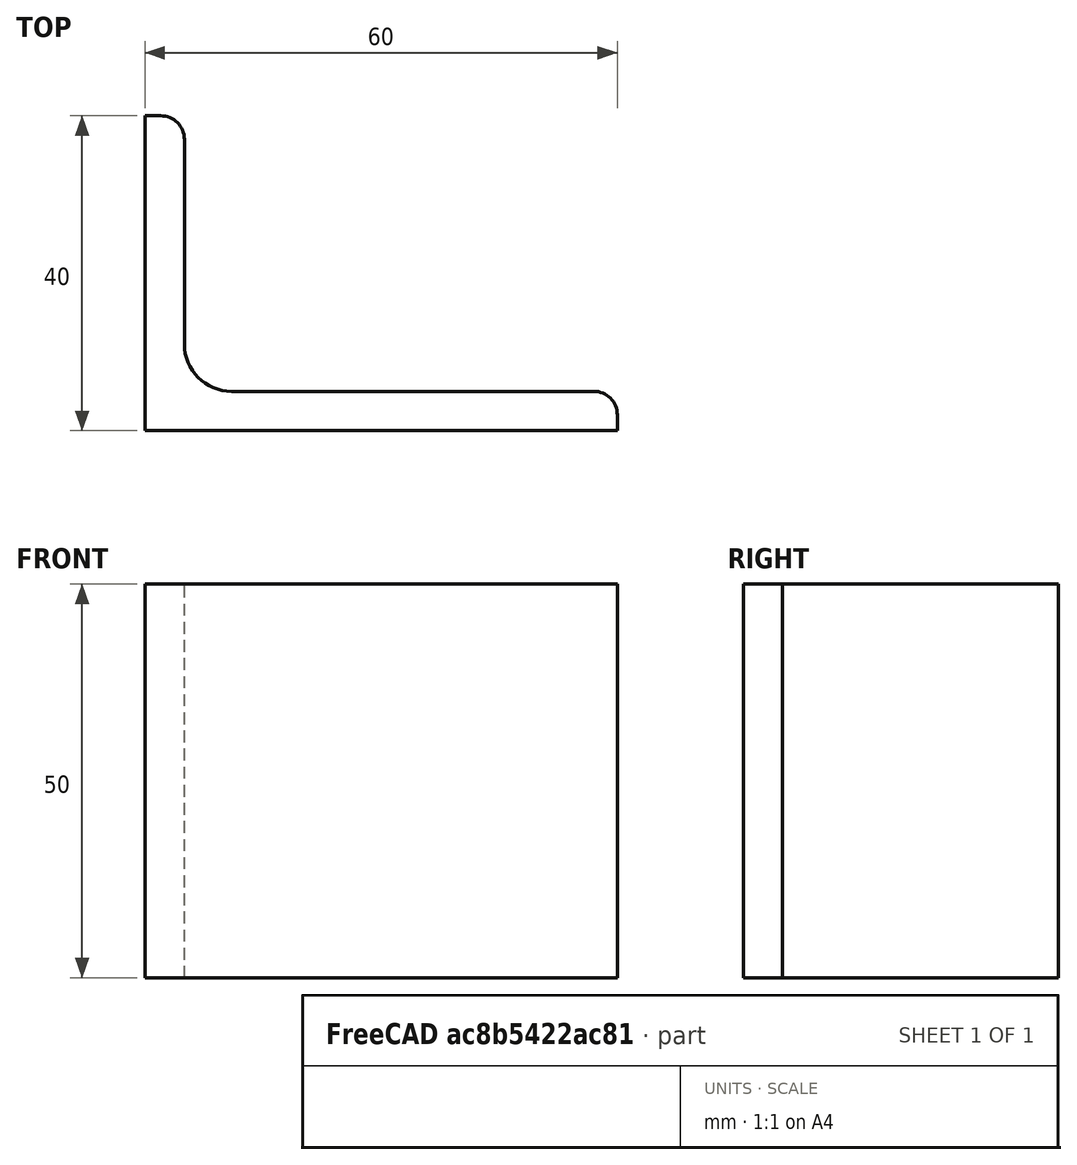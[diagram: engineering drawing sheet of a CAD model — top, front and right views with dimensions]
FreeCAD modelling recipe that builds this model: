
FCSTD DOCUMENT  (FreeCAD 0.15R4671 (Git))
Label: Angle Bar 60x40x5 EN10056 S235JR
License: All rights reserved
LicenseURL: http://en.wikipedia.org/wiki/All_rights_reserved
objects: Sketcher::SketchObject×1, Part::Extrusion×1
note: 2 computed .brp shape members not serialized (recipe doc carries the construction recipe); baked Part::Feature solids carry a one-line shape summary decoded from their .brp

FEATURE [Sketcher::SketchObject] Sketch
  sketch-geometry (9):
    g0: LineSegment StartX=0 StartY=0 StartZ=0 EndX=60 EndY=0 EndZ=0
    g1: LineSegment StartX=60 StartY=0 StartZ=0 EndX=60 EndY=2 EndZ=0
    g2: LineSegment StartX=57 StartY=5 StartZ=0 EndX=11 EndY=5 EndZ=0
    g3: LineSegment StartX=0 StartY=0 StartZ=0 EndX=0 EndY=40 EndZ=0
    g4: LineSegment StartX=0 StartY=40 StartZ=0 EndX=2 EndY=40 EndZ=0
    g5: LineSegment StartX=5 StartY=37 StartZ=0 EndX=5 EndY=11 EndZ=0
    g6: ArcOfCircle CenterX=11 CenterY=11 CenterZ=0 NormalX=0 NormalY=0 NormalZ=1 Radius=6 StartAngle=3.14159 EndAngle=4.71239
    g7: ArcOfCircle CenterX=2 CenterY=37 CenterZ=0 NormalX=0 NormalY=0 NormalZ=1 Radius=3 StartAngle=0 EndAngle=1.5708
    g8: ArcOfCircle CenterX=57 CenterY=2 CenterZ=0 NormalX=0 NormalY=0 NormalZ=1 Radius=3 StartAngle=0 EndAngle=1.5708
  constraints (23):
    c: Coincident(g0,g-1)
    c: Horizontal(g0)
    c: Coincident(g1,g0)
    c: Vertical(g1)
    c: Horizontal(g2)
    c: Coincident(g3,g-1)
    c: Vertical(g3)
    c: Coincident(g4,g3)
    c: Horizontal(g4)
    c: Vertical(g5)
    c: Tangent(g5,g6) = -1.5708
    c: Tangent(g2,g6) = 1.5708
    c: Tangent(g4,g7) = 1.5708
    c: Tangent(g5,g7) = 1.5708
    c: Tangent(g2,g8) = -1.5708
    c: Tangent(g1,g8) = -1.5708
    c: DistanceX(g0) = 60
    c: DistanceY(g3) = 40
    c: DistanceY(g0,g2) = 5
    c: DistanceX(g3,g5) = 5
    c: Radius(g6) = 6
    c: Radius(g8) = 3
    c: Radius(g7) = 3
FEATURE [Part::Extrusion] Extrude  label="Angle Bar 60x40x5 EN10056 S235JR"
  Base = -> Sketch
  Dir = (0,0,50)
  Solid = true
